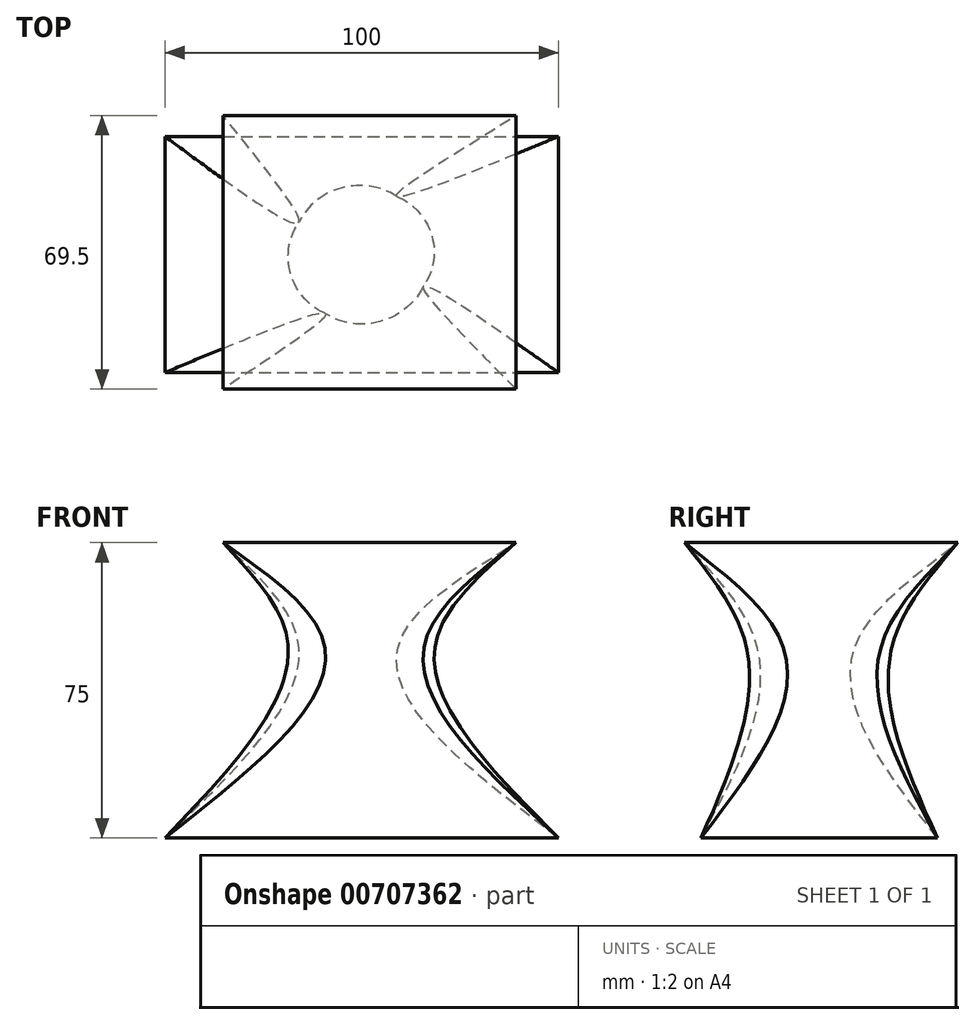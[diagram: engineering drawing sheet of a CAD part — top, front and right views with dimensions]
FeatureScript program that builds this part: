
annotation { "Feature Type Name" : "Feature", "Feature Type Description" : "" }
export const myFeature = defineFeature(function(context is Context, id is Id, definition is map)
    precondition{}
    {
        {
            var Q0;
            Q0=qCreatedBy(makeId("Top.planeOp"),FACE);
            var sketch = newSketch(context, id + "F0", { "sketchPlane" : qUnion([Q0])});
            skLineSegment(sketch, "E0.bottom", {"start": v(-50, 30) * mm, "end": v(50, 30) * mm});
            skLineSegment(sketch, "E0.top", {"start": v(-50, -30) * mm, "end": v(50, -30) * mm});
            skLineSegment(sketch, "E0.left", {"start": v(-50, 30) * mm, "end": v(-50, -30) * mm});
            skLineSegment(sketch, "E0.right", {"start": v(50, 30) * mm, "end": v(50, -30) * mm});
            skSolve(sketch);
        }
        {
            var Q0;
            Q0=qCreatedBy(makeId("Top.planeOp"),FACE);
            cPlane(context, id + "F1", {"entities" : qUnion([Q0]), "cplaneType" : CPlaneType.OFFSET, "offset" : 50 * mm, "width" : 150 * mm, "height" : 150 * mm});
        }
        {
            var Q0;
            Q0=qCreatedBy(id+"F1.planeOp",FACE);
            var sketch = newSketch(context, id + "F2", { "sketchPlane" : qUnion([Q0])});
            skCircle(sketch, "E1", {"center": v(0, 0) * mm, "radius": 18.85 * mm});
            skSolve(sketch);
        }
        {
            var Q0;
            Q0=qCreatedBy(id+"F1.planeOp",FACE);
            cPlane(context, id + "F3", {"entities" : qUnion([Q0]), "cplaneType" : CPlaneType.OFFSET, "offset" : 25 * mm, "width" : 150 * mm, "height" : 150 * mm});
        }
        {
            var Q0;
            Q0=qCreatedBy(id+"F3.planeOp",FACE);
            var sketch = newSketch(context, id + "F4", { "sketchPlane" : qUnion([Q0])});
            skLineSegment(sketch, "E2.bottom", {"start": v(39.18, 35.28) * mm, "end": v(-35.28, 35.28) * mm});
            skLineSegment(sketch, "E2.top", {"start": v(39.18, -34.22) * mm, "end": v(-35.28, -34.22) * mm});
            skLineSegment(sketch, "E2.left", {"start": v(39.18, 35.28) * mm, "end": v(39.18, -34.22) * mm});
            skLineSegment(sketch, "E2.right", {"start": v(-35.28, 35.28) * mm, "end": v(-35.28, -34.22) * mm});
            skSolve(sketch);
        }
        {
            var Q0;
            Q0=makeQuery(id+"F0.imprint","IMPRINT",FACE,{"disambiguationData":[TD([[makeQuery(id+"F0.imprint","IMPRINT",EDGE,{"derivedFrom":sQuery(id+"F0.wireOp",EDGE,"E0.bottom")}),-1.0]])]});
            var Q1;
            Q1=makeQuery(id+"F2.imprint","IMPRINT",FACE,{"disambiguationData":[TD([[makeQuery(id+"F2.imprint","IMPRINT",EDGE,{"derivedFrom":sQuery(id+"F2.wireOp",EDGE,"E1")}),1.0]])]});
            var Q2;
            Q2=makeQuery(id+"F4.imprint","IMPRINT",FACE,{"disambiguationData":[TD([[makeQuery(id+"F4.imprint","IMPRINT",EDGE,{"derivedFrom":sQuery(id+"F4.wireOp",EDGE,"E2.bottom")}),1.0]])]});
            loft(context, id + "F5", {"sheetProfilesArray" : [{ "sheetProfileEntities" : qUnion([Q0]) }, { "sheetProfileEntities" : qUnion([Q1]) }, { "sheetProfileEntities" : qUnion([Q2]) }]});
        }
        {
            var Q0;
            Q0=qCreatedBy(makeId("Right.planeOp"),FACE);
            var sketch = newSketch(context, id + "F6", { "sketchPlane" : qUnion([Q0])});
            skCircle(sketch, "E3", {"center": v(0, 43.09) * mm, "radius": 8.8 * mm});
            skSolve(sketch);
        }
        {
            var Q0;
            Q0=sQuery(id+"F6.wireOp",EDGE,"E3");
            extrude(context, id + "F7", {"bodyType" : ToolBodyType.SURFACE, "surfaceEntities" : qUnion([Q0]), "depth" : 50 * mm, "offsetDistance" : 25 * mm});
        }
    });
